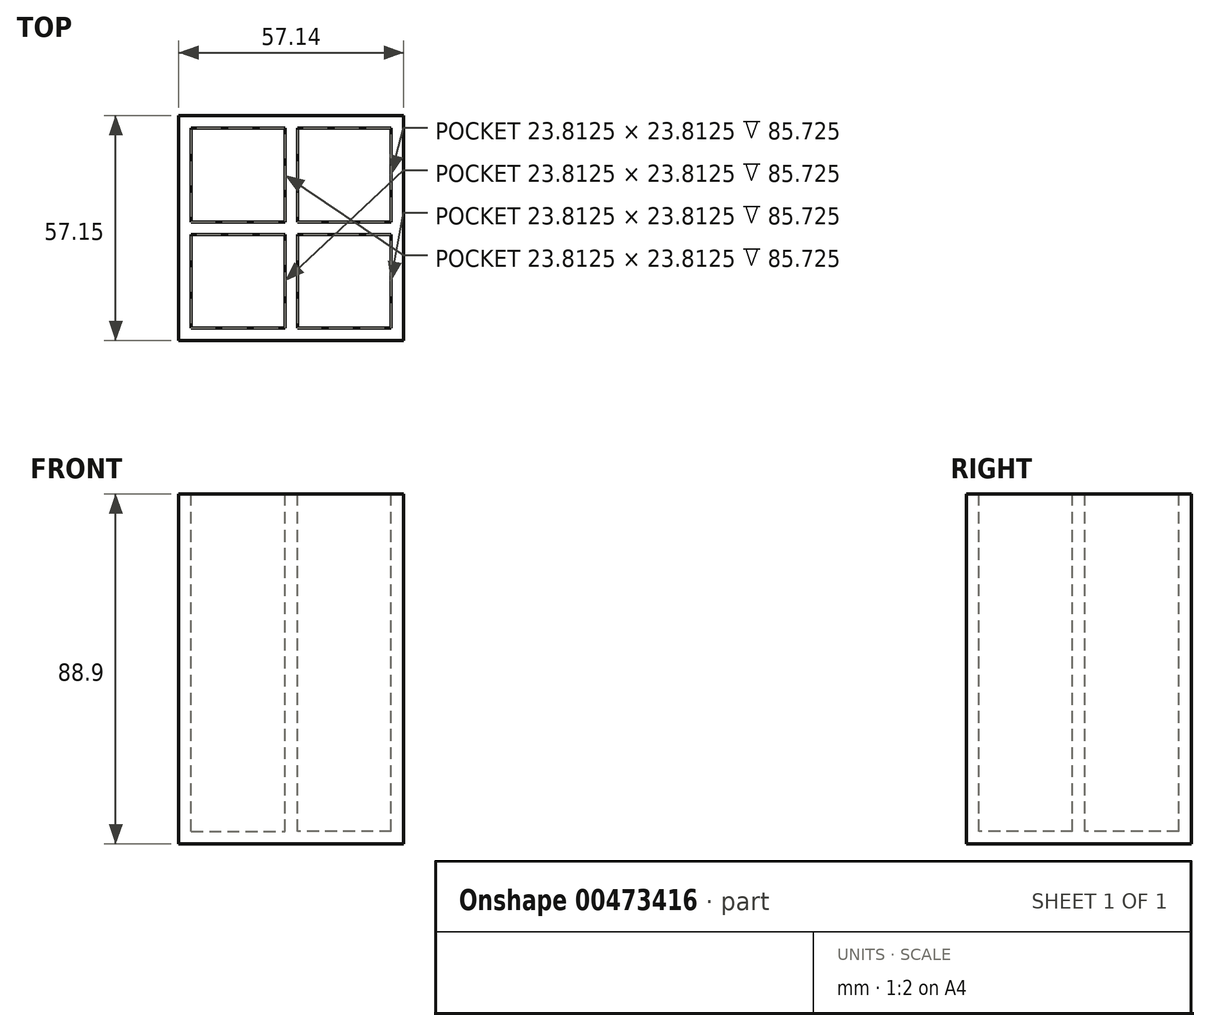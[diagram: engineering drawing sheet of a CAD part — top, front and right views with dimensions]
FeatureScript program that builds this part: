
annotation { "Feature Type Name" : "Feature", "Feature Type Description" : "" }
export const myFeature = defineFeature(function(context is Context, id is Id, definition is map)
    precondition{}
    {
        {
            var Q0;
            Q0=qCreatedBy(makeId("Front.planeOp"),FACE);
            var sketch = newSketch(context, id + "F0", { "sketchPlane" : qUnion([Q0])});
            skLineSegment(sketch, "E0.bottom", {"start": v(28.57, 44.45) * mm, "end": v(-28.58, 44.45) * mm});
            skLineSegment(sketch, "E0.top", {"start": v(28.58, -44.45) * mm, "end": v(-28.57, -44.45) * mm});
            skLineSegment(sketch, "E0.left", {"start": v(28.57, 44.45) * mm, "end": v(28.58, -44.45) * mm});
            skLineSegment(sketch, "E0.right", {"start": v(-28.58, 44.45) * mm, "end": v(-28.57, -44.45) * mm});
            skPoint(sketch, "E0.middle", {"position": v(0, 0) * mm});
            skSolve(sketch);
        }
        {
            var Q0;
            Q0 = qSketchRegion(id + "F0", true);
            extrude(context, id + "F1", {"entities" : qUnion([Q0]), "depth" : 57.15 * mm});
        }
        {
            var Q0;
            Q0=makeQuery(id+"F1.opExtrude","SWEPT_FACE",FACE,{"disambiguationData":[OSD([sQuery(id+"F0.wireOp",EDGE,"E0.bottom")])]});
            var sketch = newSketch(context, id + "F2", { "sketchPlane" : qUnion([Q0])});
            skPoint(sketch, "E1.middle", {"position": v(0, 0) * mm});
            skLineSegment(sketch, "E2", {"start": v(25.4, -3.18) * mm, "end": v(1.59, -3.18) * mm});
            skLineSegment(sketch, "E3", {"start": v(-1.59, -3.18) * mm, "end": v(-25.4, -3.18) * mm});
            skLineSegment(sketch, "E4", {"start": v(1.59, -3.18) * mm, "end": v(1.59, -26.99) * mm});
            skLineSegment(sketch, "E5", {"start": v(-1.59, -3.18) * mm, "end": v(-1.59, -26.99) * mm});
            skLineSegment(sketch, "E6", {"start": v(25.4, -30.16) * mm, "end": v(25.4, -53.98) * mm});
            skLineSegment(sketch, "E7", {"start": v(1.59, -53.98) * mm, "end": v(25.4, -53.98) * mm});
            skLineSegment(sketch, "E8", {"start": v(-25.4, -3.17) * mm, "end": v(-25.4, -26.99) * mm});
            skLineSegment(sketch, "E9", {"start": v(-1.59, -53.98) * mm, "end": v(-25.4, -53.98) * mm});
            skLineSegment(sketch, "E10", {"start": v(25.4, -3.18) * mm, "end": v(25.4, -26.99) * mm});
            skLineSegment(sketch, "E11", {"start": v(25.4, -26.99) * mm, "end": v(1.59, -26.99) * mm});
            skLineSegment(sketch, "E12", {"start": v(25.4, -30.16) * mm, "end": v(1.59, -30.16) * mm});
            skLineSegment(sketch, "E13.bottom", {"start": v(-25.4, -30.16) * mm, "end": v(-1.59, -30.16) * mm});
            skLineSegment(sketch, "E13.top", {"start": v(-25.4, -53.98) * mm, "end": v(-1.59, -53.98) * mm});
            skLineSegment(sketch, "E13.left", {"start": v(-25.4, -30.16) * mm, "end": v(-25.4, -53.98) * mm});
            skLineSegment(sketch, "E13.right", {"start": v(-1.59, -30.16) * mm, "end": v(-1.59, -53.98) * mm});
            skLineSegment(sketch, "E14.top", {"start": v(25.4, -53.98) * mm, "end": v(1.59, -53.98) * mm});
            skLineSegment(sketch, "E14.right", {"start": v(1.59, -30.16) * mm, "end": v(1.59, -53.98) * mm});
            skLineSegment(sketch, "E15.left", {"start": v(25.4, -26.99) * mm, "end": v(25.4, -3.18) * mm});
            skLineSegment(sketch, "E15.right", {"start": v(1.59, -26.99) * mm, "end": v(1.59, -3.18) * mm});
            skLineSegment(sketch, "E16.bottom", {"start": v(-25.4, -3.18) * mm, "end": v(-1.59, -3.18) * mm});
            skLineSegment(sketch, "E16.top", {"start": v(-25.4, -26.99) * mm, "end": v(-1.59, -26.99) * mm});
            skLineSegment(sketch, "E16.left", {"start": v(-25.4, -3.18) * mm, "end": v(-25.4, -26.99) * mm});
            skLineSegment(sketch, "E17.trimOffspring", {"start": v(-1.59, -26.99) * mm, "end": v(-25.4, -26.99) * mm});
            skLineSegment(sketch, "E18.trimOffspring", {"start": v(-1.59, -30.16) * mm, "end": v(-25.4, -30.16) * mm});
            skSolve(sketch);
        }
        {
            var Q0;
            Q0 = qSketchRegion(id + "F2", true);
            extrude(context, id + "F3", {"entities" : qUnion([Q0]), "operationType" : NewBodyOperationType.REMOVE, "oppositeDirection" : true, "depth" : 85.72 * mm});
        }
    });
